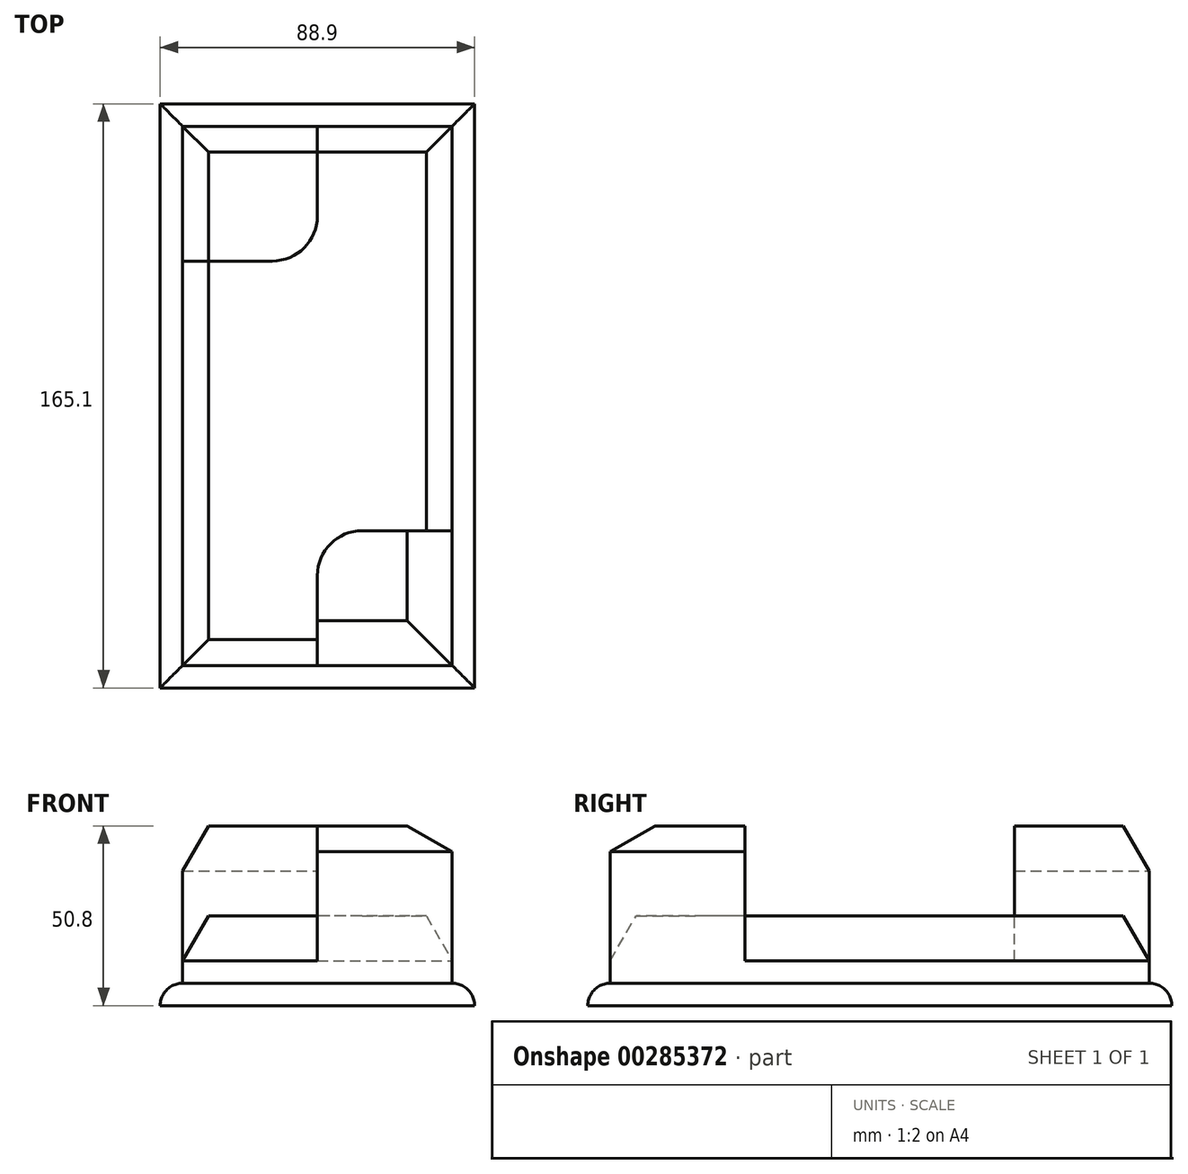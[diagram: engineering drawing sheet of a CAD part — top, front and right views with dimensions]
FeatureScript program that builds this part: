
annotation { "Feature Type Name" : "Feature", "Feature Type Description" : "" }
export const myFeature = defineFeature(function(context is Context, id is Id, definition is map)
    precondition{}
    {
        {
            var Q0;
            Q0=qCreatedBy(makeId("Top.planeOp"),FACE);
            var sketch = newSketch(context, id + "F0", { "sketchPlane" : qUnion([Q0])});
            skLineSegment(sketch, "E0.bottom", {"start": v(38.1, 76.2) * mm, "end": v(-38.1, 76.2) * mm});
            skLineSegment(sketch, "E0.top", {"start": v(38.1, -76.2) * mm, "end": v(-38.1, -76.2) * mm});
            skLineSegment(sketch, "E0.left", {"start": v(38.1, 76.2) * mm, "end": v(38.1, -76.2) * mm});
            skLineSegment(sketch, "E0.right", {"start": v(-38.1, 76.2) * mm, "end": v(-38.1, -76.2) * mm});
            skPoint(sketch, "E0.middle", {"position": v(0, 0) * mm});
            skLineSegment(sketch, "E1.0", {"start": v(-44.45, 82.55) * mm, "end": v(-44.45, -82.55) * mm});
            skLineSegment(sketch, "E1.1", {"start": v(44.45, 82.55) * mm, "end": v(-44.45, 82.55) * mm});
            skLineSegment(sketch, "E1.2", {"start": v(44.45, 82.55) * mm, "end": v(44.45, -82.55) * mm});
            skLineSegment(sketch, "E1.3", {"start": v(44.45, -82.55) * mm, "end": v(-44.45, -82.55) * mm});
            skLineSegment(sketch, "E2", {"start": v(0, 76.2) * mm, "end": v(0, 50.8) * mm});
            skLineSegment(sketch, "E3", {"start": v(-12.7, 38.1) * mm, "end": v(-38.1, 38.1) * mm});
            skLineSegment(sketch, "E4", {"start": v(0, -76.2) * mm, "end": v(0, -50.8) * mm});
            skPoint(sketch, "E4.endSnap0", {"position": v(0, -76.2) * mm});
            skLineSegment(sketch, "E5", {"start": v(12.7, -38.1) * mm, "end": v(38.1, -38.1) * mm});
            skPoint(sketch, "E6.visualSharp", {"position": v(0, 38.1) * mm});
            skArc(sketch, "E6.filletArc", {"start": v(-12.7, 38.1) * mm, "mid": v(-3.72, 41.82) * mm, "end": v(0, 50.8) * mm});
            skPoint(sketch, "E7.visualSharp", {"position": v(0, -38.1) * mm});
            skArc(sketch, "E7.filletArc", {"start": v(12.7, -38.1) * mm, "mid": v(3.72, -41.82) * mm, "end": v(0, -50.8) * mm});
            skSolve(sketch);
        }
        {
            var Q0;
            Q0=makeQuery(id+"F0.imprint","IMPRINT",FACE,{"disambiguationData":[TD([[makeQuery(id+"F0.imprint","IMPRINT",EDGE,{"derivedFrom":sQuery(id+"F0.wireOp",EDGE,"E1.0")}),1.0]])]});
            extrude(context, id + "F1", {"entities" : qUnion([Q0]), "depth" : 6.35 * mm});
        }
        {
            var Q0;
            {var subQ9=sQuery(id+"F0.wireOp",EDGE,"E2");Q0=makeQuery(id+"F0.imprint","IMPRINT",FACE,{"disambiguationData":[TD([[makeQuery(id+"F0.imprint","IMPRINT",EDGE,{"derivedFrom":subQ9}),1.0]])]});}
            extrude(context, id + "F2", {"entities" : qUnion([Q0]), "operationType" : NewBodyOperationType.ADD, "depth" : 25.4 * mm});
        }
        {
            var Q0;
            {var subQ1=sQuery(id+"F0.wireOp",EDGE,"E2");Q0=makeQuery(id+"F0.imprint","IMPRINT",FACE,{"disambiguationData":[TD([[makeQuery(id+"F0.imprint","IMPRINT",EDGE,{"derivedFrom":subQ1}),-1.0]])]});}
            var Q1;
            {var subQ0=sQuery(id+"F0.wireOp",EDGE,"E4");Q1=makeQuery(id+"F0.imprint","IMPRINT",FACE,{"disambiguationData":[TD([[makeQuery(id+"F0.imprint","IMPRINT",EDGE,{"derivedFrom":subQ0}),-1.0]])]});}
            extrude(context, id + "F3", {"entities" : qUnion([Q0, Q1]), "operationType" : NewBodyOperationType.ADD, "depth" : 50.8 * mm});
        }
        {
            var Q0;
            Q0=makeQuery(id+"F2.opExtrude","CAP_EDGE",EDGE,{"disambiguationData":[OSD([sQuery(id+"F0.wireOp",EDGE,"E0.right")])],"isStart":false});
            var Q1;
            Q1=makeQuery(id+"F2.opExtrude","CAP_EDGE",EDGE,{"disambiguationData":[OSD([sQuery(id+"F0.wireOp",EDGE,"E0.top")])],"isStart":false});
            var Q2;
            Q2=makeQuery(id+"F2.opExtrude","CAP_EDGE",EDGE,{"disambiguationData":[OSD([sQuery(id+"F0.wireOp",EDGE,"E0.bottom")])],"isStart":false});
            var Q3;
            Q3=makeQuery(id+"F2.opExtrude","CAP_EDGE",EDGE,{"disambiguationData":[OSD([sQuery(id+"F0.wireOp",EDGE,"E0.left")])],"isStart":false});
            var Q4;
            Q4=makeQuery(id+"F3.opExtrude","CAP_EDGE",EDGE,{"disambiguationData":[OSD([sQuery(id+"F0.wireOp",EDGE,"E0.bottom")])],"isStart":false});
            var Q5;
            Q5=makeQuery(id+"F3.opExtrude","CAP_EDGE",EDGE,{"disambiguationData":[OSD([sQuery(id+"F0.wireOp",EDGE,"E0.right")])],"isStart":false});
            var Q6;
            Q6=makeQuery(id+"F3.opExtrude","CAP_EDGE",EDGE,{"disambiguationData":[OSD([sQuery(id+"F0.wireOp",EDGE,"E0.left")])],"isStart":false});
            var Q7;
            Q7=makeQuery(id+"F3.opExtrude","CAP_EDGE",EDGE,{"disambiguationData":[OSD([sQuery(id+"F0.wireOp",EDGE,"E0.top")])],"isStart":false});
            chamfer(context, id + "F4", {"entities" : qUnion([Q0, Q1, Q2, Q3, Q4, Q5, Q6, Q7]), "chamferType" : ChamferType.OFFSET_ANGLE, "width" : 12.7 * mm, "oppositeDirection" : true, "angle" : 30 * degree});
        }
        {
            var Q0;
            Q0=makeQuery(id+"F1.opExtrude","CAP_EDGE",EDGE,{"disambiguationData":[OSD([sQuery(id+"F0.wireOp",EDGE,"E1.3")])],"isStart":false});
            var Q1;
            Q1=makeQuery(id+"F1.opExtrude","CAP_EDGE",EDGE,{"disambiguationData":[OSD([sQuery(id+"F0.wireOp",EDGE,"E1.0")])],"isStart":false});
            var Q2;
            Q2=makeQuery(id+"F1.opExtrude","CAP_EDGE",EDGE,{"disambiguationData":[OSD([sQuery(id+"F0.wireOp",EDGE,"E1.2")])],"isStart":false});
            var Q3;
            Q3=makeQuery(id+"F1.opExtrude","CAP_EDGE",EDGE,{"disambiguationData":[OSD([sQuery(id+"F0.wireOp",EDGE,"E1.1")])],"isStart":false});
            fillet(context, id + "F5", {"entities" : qUnion([Q0, Q1, Q2, Q3]), "radius" : 6.35 * mm, "tangentPropagation" : true, "allowEdgeOverflow" : false});
        }
    });
